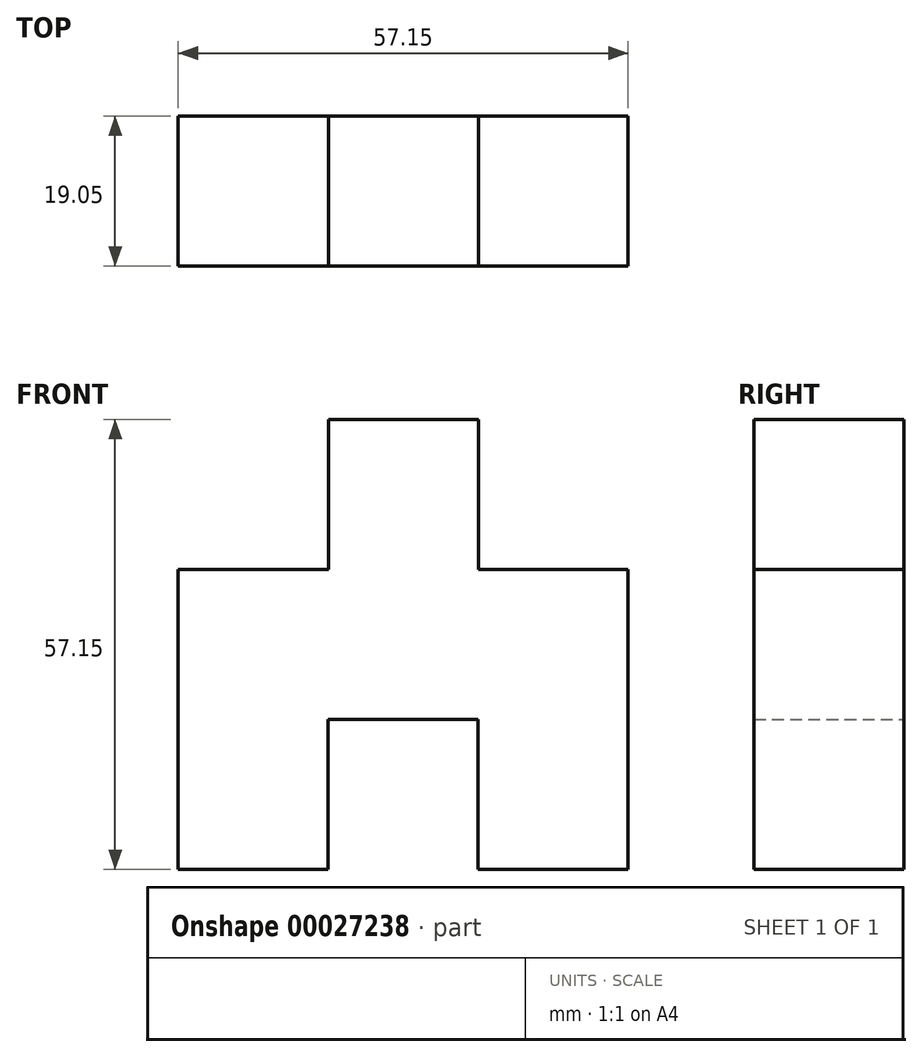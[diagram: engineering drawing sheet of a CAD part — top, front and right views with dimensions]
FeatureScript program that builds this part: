
annotation { "Feature Type Name" : "Feature", "Feature Type Description" : "" }
export const myFeature = defineFeature(function(context is Context, id is Id, definition is map)
    precondition{}
    {
        {
            var Q0;
            Q0=qCreatedBy(makeId("Top.planeOp"),FACE);
            var sketch = newSketch(context, id + "F0", { "sketchPlane" : qUnion([Q0])});
            skLineSegment(sketch, "E0.bottom", {"start": v(-54.72, 19.05) * mm, "end": v(2.43, 19.05) * mm});
            skLineSegment(sketch, "E0.top", {"start": v(-54.72, 0) * mm, "end": v(2.43, 0) * mm});
            skLineSegment(sketch, "E0.left", {"start": v(-54.72, 19.05) * mm, "end": v(-54.72, 0) * mm});
            skLineSegment(sketch, "E0.right", {"start": v(2.43, 19.05) * mm, "end": v(2.43, 0) * mm});
            skSolve(sketch);
        }
        {
            var Q0;
            Q0=makeQuery(id+"F0.imprint","IMPRINT",FACE,{"disambiguationData":[TD([[makeQuery(id+"F0.imprint","IMPRINT",EDGE,{"derivedFrom":sQuery(id+"F0.wireOp",EDGE,"E0.bottom")}),-1.0]])]});
            extrude(context, id + "F1", {"entities" : qUnion([Q0]), "depth" : 19.05 * mm});
        }
        {
            var Q0;
            Q0=makeQuery(id+"F1.opExtrude","CAP_FACE",FACE,{"disambiguationData":[OSD([sQuery(id+"F0.wireOp",EDGE,"E0.bottom"),sQuery(id+"F0.wireOp",EDGE,"E0.top"),sQuery(id+"F0.wireOp",EDGE,"E0.left"),sQuery(id+"F0.wireOp",EDGE,"E0.right")])],"isStart":false});
            var sketch = newSketch(context, id + "F2", { "sketchPlane" : qUnion([Q0])});
            skLineSegment(sketch, "E1.bottom", {"start": v(-35.61, 19.05) * mm, "end": v(-16.56, 19.05) * mm});
            skLineSegment(sketch, "E1.top", {"start": v(-35.61, 0) * mm, "end": v(-16.56, 0) * mm});
            skLineSegment(sketch, "E1.left", {"start": v(-35.61, 19.05) * mm, "end": v(-35.61, 0) * mm});
            skLineSegment(sketch, "E1.right", {"start": v(-16.56, 19.05) * mm, "end": v(-16.56, 0) * mm});
            skSolve(sketch);
        }
        {
            var Q0;
            Q0=makeQuery(id+"F2.imprint","IMPRINT",FACE,{"disambiguationData":[TD([[makeQuery(id+"F2.imprint","IMPRINT",EDGE,{"derivedFrom":sQuery(id+"F2.wireOp",EDGE,"E1.bottom")}),-1.0]])]});
            extrude(context, id + "F3", {"entities" : qUnion([Q0]), "operationType" : NewBodyOperationType.ADD, "depth" : 19.05 * mm});
        }
        {
            var Q0;
            Q0=makeQuery(id+"F1.opExtrude","CAP_FACE",FACE,{"disambiguationData":[OSD([sQuery(id+"F0.wireOp",EDGE,"E0.bottom"),sQuery(id+"F0.wireOp",EDGE,"E0.top"),sQuery(id+"F0.wireOp",EDGE,"E0.left"),sQuery(id+"F0.wireOp",EDGE,"E0.right")])],"isStart":true});
            var sketch = newSketch(context, id + "F4", { "sketchPlane" : qUnion([Q0])});
            skLineSegment(sketch, "E2.bottom", {"start": v(-54.72, 0) * mm, "end": v(-35.67, 0) * mm});
            skLineSegment(sketch, "E2.top", {"start": v(-54.72, -19.05) * mm, "end": v(-35.67, -19.05) * mm});
            skLineSegment(sketch, "E2.left", {"start": v(-54.72, 0) * mm, "end": v(-54.72, -19.05) * mm});
            skLineSegment(sketch, "E2.right", {"start": v(-35.67, 0) * mm, "end": v(-35.67, -19.05) * mm});
            skLineSegment(sketch, "E3.bottom", {"start": v(2.43, 0) * mm, "end": v(-16.62, 0) * mm});
            skLineSegment(sketch, "E3.top", {"start": v(2.43, -19.05) * mm, "end": v(-16.62, -19.05) * mm});
            skLineSegment(sketch, "E3.left", {"start": v(2.43, 0) * mm, "end": v(2.43, -19.05) * mm});
            skLineSegment(sketch, "E3.right", {"start": v(-16.62, 0) * mm, "end": v(-16.62, -19.05) * mm});
            skSolve(sketch);
        }
        {
            var Q0;
            Q0=makeQuery(id+"F4.imprint","IMPRINT",FACE,{"disambiguationData":[TD([[makeQuery(id+"F4.imprint","IMPRINT",EDGE,{"derivedFrom":sQuery(id+"F4.wireOp",EDGE,"E3.bottom")}),-1.0]])]});
            var Q1;
            Q1=makeQuery(id+"F4.imprint","IMPRINT",FACE,{"disambiguationData":[TD([[makeQuery(id+"F4.imprint","IMPRINT",EDGE,{"derivedFrom":sQuery(id+"F4.wireOp",EDGE,"E2.bottom")}),-1.0]])]});
            extrude(context, id + "F5", {"entities" : qUnion([Q0, Q1]), "operationType" : NewBodyOperationType.ADD, "depth" : 19.05 * mm});
        }
    });
